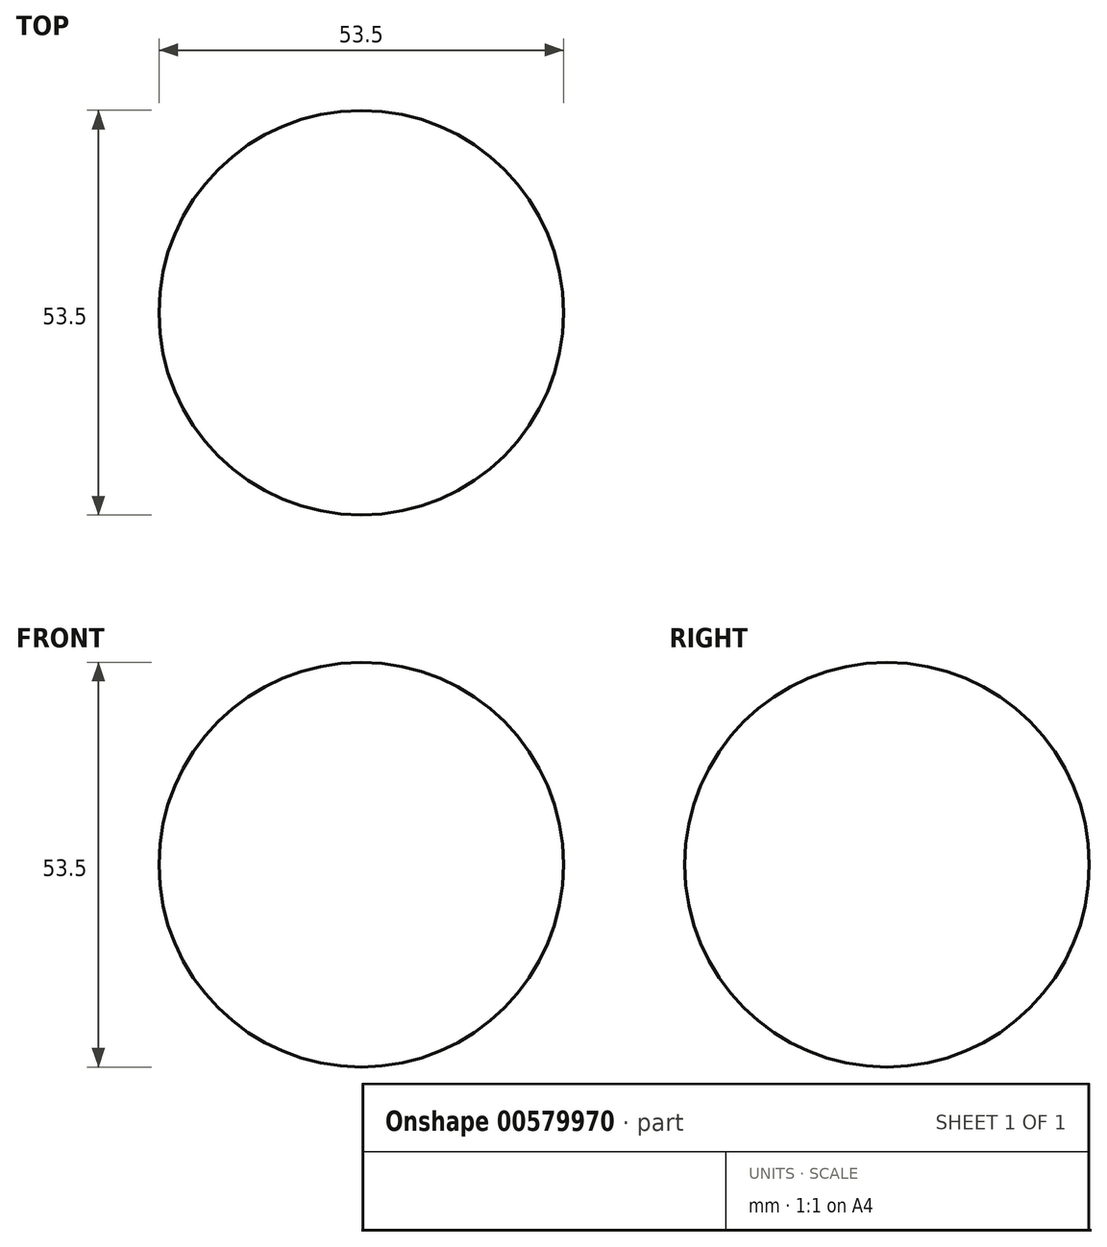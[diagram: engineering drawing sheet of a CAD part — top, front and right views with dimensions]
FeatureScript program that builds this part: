
annotation { "Feature Type Name" : "Feature", "Feature Type Description" : "" }
export const myFeature = defineFeature(function(context is Context, id is Id, definition is map)
    precondition{}
    {
        {
            var Q0;
            Q0=qCreatedBy(makeId("Front.planeOp"),FACE);
            var sketch = newSketch(context, id + "F0", { "sketchPlane" : qUnion([Q0])});
            skArc(sketch, "E0", {"start": v(0, 26.75) * mm, "mid": v(-26.75, 0) * mm, "end": v(0, -26.75) * mm});
            skLineSegment(sketch, "E1", {"start": v(0, 26.75) * mm, "end": v(0, -26.75) * mm});
            skSolve(sketch);
        }
        {
            var Q0;
            Q0=makeQuery(id+"F0.imprint","IMPRINT",FACE,{"disambiguationData":[TD([[makeQuery(id+"F0.imprint","IMPRINT",EDGE,{"derivedFrom":sQuery(id+"F0.wireOp",EDGE,"E0")}),1.0]])]});
            var Q1;
            Q1=sQuery(id+"F0.wireOp",EDGE,"E1");
            revolve(context, id + "F1", {"entities" : qUnion([Q0]), "axis" : qUnion([Q1]), "revolveType" : RevolveType.FULL});
        }
    });
